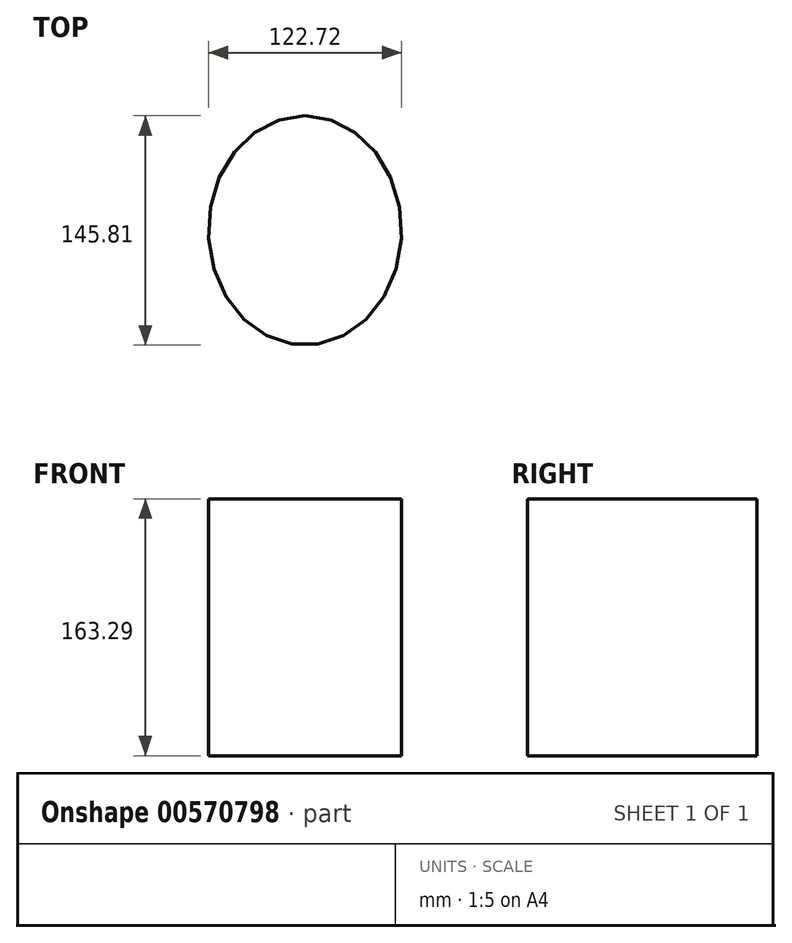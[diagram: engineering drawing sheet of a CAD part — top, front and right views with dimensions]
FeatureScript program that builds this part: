
annotation { "Feature Type Name" : "Feature", "Feature Type Description" : "" }
export const myFeature = defineFeature(function(context is Context, id is Id, definition is map)
    precondition{}
    {
        {
            var Q0;
            Q0=qCreatedBy(makeId("Top.planeOp"),FACE);
            var sketch = newSketch(context, id + "F0", { "sketchPlane" : qUnion([Q0])});
            skEllipse(sketch, "E0", {"center": v(0, -49.44) * mm, "majorRadius": 61.36 * mm, "minorRadius": 72.9 * mm, "majorAxis": v(1, 0)});
            skSolve(sketch);
        }
        {
            var Q0;
            Q0=makeQuery(id+"F0.imprint","IMPRINT",FACE,{"disambiguationData":[TD([[makeQuery(id+"F0.imprint","IMPRINT",EDGE,{"derivedFrom":sQuery(id+"F0.wireOp",EDGE,"E0")}),1.0]])]});
            extrude(context, id + "F1", {"entities" : qUnion([Q0]), "depth" : 163.3 * mm, "offsetDistance" : 25.4 * mm});
        }
    });
